# Revit family: Switch-Lutron-HomeWork-Wired_Alisse_Keypad
name_source: partatom
category: Lighting Devices
revit_build: Autodesk Revit 2018 (Build: 20190510_1515(x64)
units: mm (PartAtom-declared; Revit-internal decimal feet)

## family parameters
Cut with Voids When Loaded = No
Host = Face
Maintain Annotation Orientation = Yes
OmniClass Number = 23.85.80.11.27
OmniClass Title = Lighting Controls
Part Type = Switch
Room Calculation Point = No
Round Connector Dimension = Use Diameter
Shared = No

## types (3) — shared parameters
Additional Material Finish = Metal - Lutron - Aged Brass
Assembly Code = D5020120
Default Elevation = 4' - 0"
Description = HomeWorks Wired Alisse Keypad
Engraved = No
Environment = Ambient operating temperature: 32 °F to 104 °F (0 °C to 40 °C), 0% to 90% non-condensing relative humidity. Indoor use only.
Insert = No
Instruction Sheet Link = https://www.lutron.com
Instruction Sheet Link - QS Keypad Base Unit = https://www.lutron.com
Manufacturer = Lutron Electronics Co., Inc
Manufacturer Fax Number = 610-282-1243
Overall Depth = 0' - 1 9/32"
Overall Height = 0' - 3 9/16"
Performance URL = https://www.lutron.com
Product Documentation Link = https://www.lutron.com
Product Name = Alisse Keypad
Product Page URL = https://www.lutron.com
Series = HomeWorks
URL = http://www.lutron.com
Version = 2018 - v1.0a
Video Link = https://www.youtube.com
Voltage = 24 V
Voltage Comment = 24-36V
Wallstation Material = Metal - Lutron - Aged Brass
Warranty URL = http://www.lutron.com
zero-valued in all types: Cost

## per-type parameters (varying)
| type | 1-Column | 2-Column | 3-Column | Constraints | Model | Overall Width | Wattage Comment |
| Single Column Keypad and Base Unit | Yes | No | No | 1 | HW–NW–KP–S1 + HW–QS–B–S1 | 0' - 3 9/16" | 370 mW |
| Two Column Keypad and Base Unit | No | Yes | No | 2 | HW–NW–KP–S2 + HW–QS–B–S1 | 0' - 3 9/16" | 449 mW |
| Three Column Keypad and Base Unit | No | No | Yes | 3 | HW–NW–KP–S3 + HW–QS–B–S3 | 0' - 4 13/16" | 543 mW |

## geometry (parser evidence)
native form markers: Sweep x6
no freeform markers — native parametric forms only
